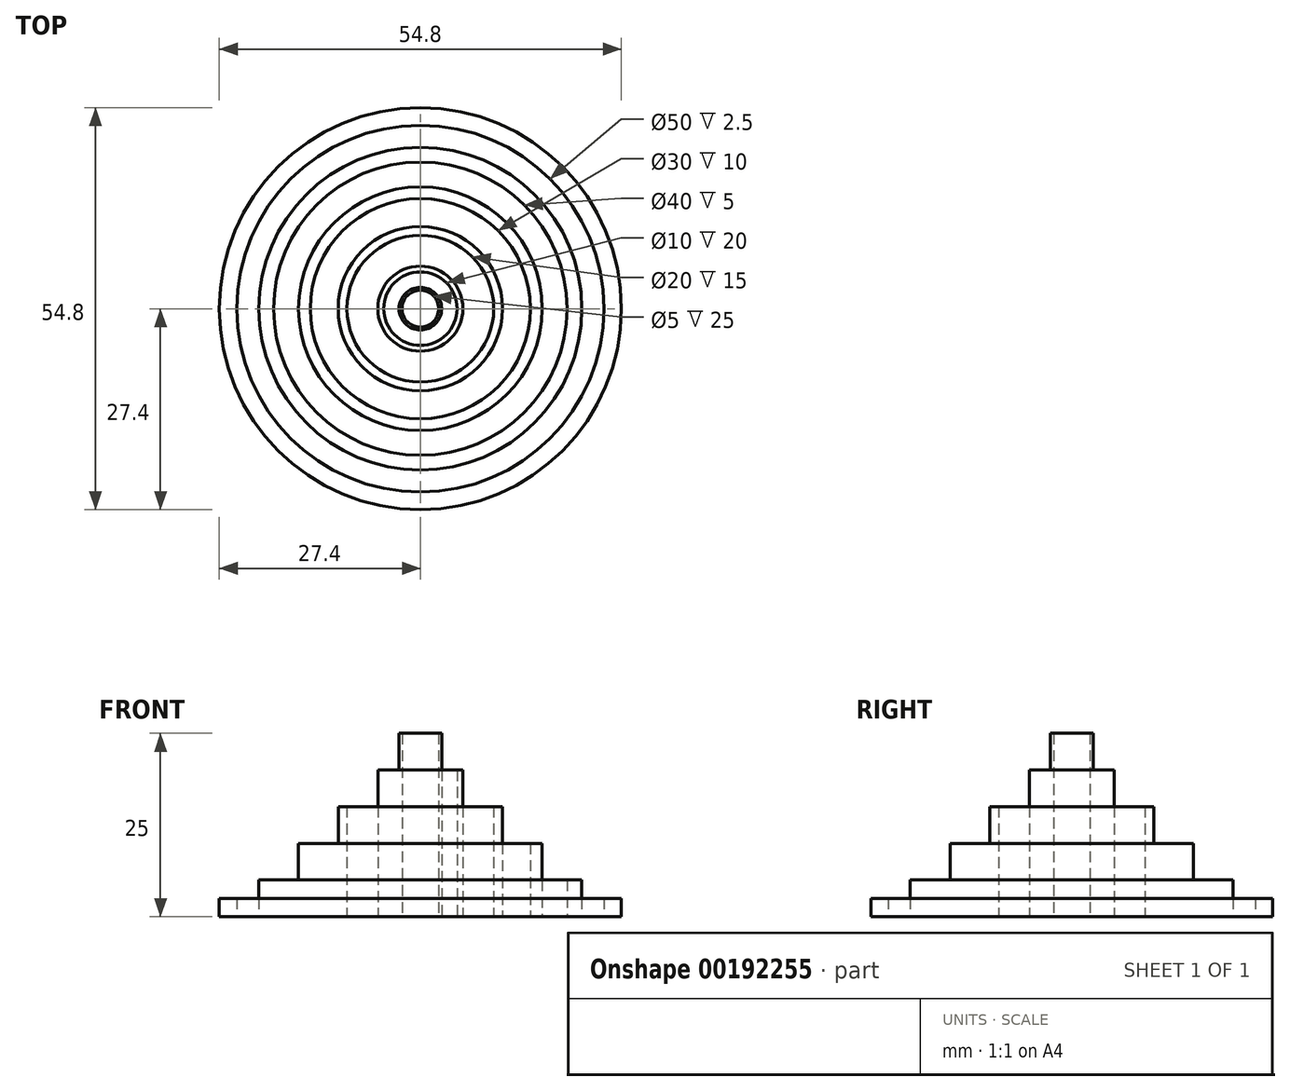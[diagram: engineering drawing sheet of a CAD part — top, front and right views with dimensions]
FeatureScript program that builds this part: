
annotation { "Feature Type Name" : "Feature", "Feature Type Description" : "" }
export const myFeature = defineFeature(function(context is Context, id is Id, definition is map)
    precondition{}
    {
        {
            var Q0;
            Q0=qCreatedBy(makeId("Top.planeOp"),FACE);
            var sketch = newSketch(context, id + "F0", { "sketchPlane" : qUnion([Q0])});
            skCircle(sketch, "E0", {"center": v(0, 0) * mm, "radius": 2.9 * mm});
            skCircle(sketch, "E1", {"center": v(0, 0) * mm, "radius": 2.5 * mm});
            skCircle(sketch, "E2", {"center": v(0, 0) * mm, "radius": 5 * mm});
            skCircle(sketch, "E3", {"center": v(0, 0) * mm, "radius": 5.8 * mm});
            skCircle(sketch, "E4", {"center": v(0, 0) * mm, "radius": 10 * mm});
            skCircle(sketch, "E5", {"center": v(0, 0) * mm, "radius": 11.2 * mm});
            skCircle(sketch, "E6", {"center": v(0, 0) * mm, "radius": 15 * mm});
            skCircle(sketch, "E7", {"center": v(0, 0) * mm, "radius": 16.6 * mm});
            skCircle(sketch, "E8", {"center": v(0, 0) * mm, "radius": 20 * mm});
            skCircle(sketch, "E9", {"center": v(0, 0) * mm, "radius": 22 * mm});
            skLineSegment(sketch, "E10", {"start": v(0, 0) * mm, "end": v(0, 35.96) * mm, "construction": true});
            skCircle(sketch, "E11", {"center": v(0, 0) * mm, "radius": 25 * mm});
            skCircle(sketch, "E12", {"center": v(0, 0) * mm, "radius": 27.4 * mm});
            skSolve(sketch);
        }
        {
            var Q0;
            Q0=makeQuery(id+"F0.imprint","IMPRINT",FACE,{"disambiguationData":[TD([[makeQuery(id+"F0.imprint","IMPRINT",EDGE,{"derivedFrom":sQuery(id+"F0.wireOp",EDGE,"E0")}),1.0]])]});
            extrude(context, id + "F1", {"entities" : qUnion([Q0]), "depth" : 25 * mm});
        }
        {
            var Q0;
            Q0=makeQuery(id+"F0.imprint","IMPRINT",FACE,{"disambiguationData":[TD([[makeQuery(id+"F0.imprint","IMPRINT",EDGE,{"derivedFrom":sQuery(id+"F0.wireOp",EDGE,"E2")}),-1.0]])]});
            extrude(context, id + "F2", {"entities" : qUnion([Q0]), "depth" : 20 * mm});
        }
        {
            var Q0;
            Q0=makeQuery(id+"F0.imprint","IMPRINT",FACE,{"disambiguationData":[TD([[makeQuery(id+"F0.imprint","IMPRINT",EDGE,{"derivedFrom":sQuery(id+"F0.wireOp",EDGE,"E4")}),-1.0]])]});
            extrude(context, id + "F3", {"entities" : qUnion([Q0]), "depth" : 15 * mm});
        }
        {
            var Q0;
            Q0=makeQuery(id+"F0.imprint","IMPRINT",FACE,{"disambiguationData":[TD([[makeQuery(id+"F0.imprint","IMPRINT",EDGE,{"derivedFrom":sQuery(id+"F0.wireOp",EDGE,"E6")}),-1.0]])]});
            extrude(context, id + "F4", {"entities" : qUnion([Q0]), "depth" : 10 * mm});
        }
        {
            var Q0;
            Q0=makeQuery(id+"F0.imprint","IMPRINT",FACE,{"disambiguationData":[TD([[makeQuery(id+"F0.imprint","IMPRINT",EDGE,{"derivedFrom":sQuery(id+"F0.wireOp",EDGE,"E8")}),-1.0]])]});
            extrude(context, id + "F5", {"entities" : qUnion([Q0]), "depth" : 5 * mm});
        }
        {
            var Q0;
            Q0=makeQuery(id+"F0.imprint","IMPRINT",FACE,{"disambiguationData":[TD([[makeQuery(id+"F0.imprint","IMPRINT",EDGE,{"derivedFrom":sQuery(id+"F0.wireOp",EDGE,"E11")}),-1.0]])]});
            extrude(context, id + "F6", {"entities" : qUnion([Q0]), "depth" : 2.5 * mm});
        }
    });
